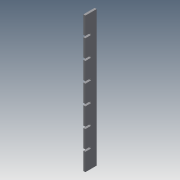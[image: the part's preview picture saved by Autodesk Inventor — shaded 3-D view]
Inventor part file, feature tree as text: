
AUTODESK INVENTOR PART (.ipt)
format: ipt  version: 2015 (Build 190159000, 159)  size: 107,520 bytes
history: native  units: mm
features: extrude x1
ambient origin geometry x8: Origin, YZ Plane, XZ Plane, XY Plane, X Axis, Y Axis, Z Axis, Center Point
bodies: Body1 (feature_tree)
feature tree (1):
  extrude  "Extrusion2"  Depth=50.0mm
